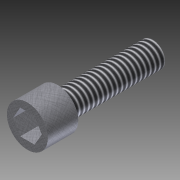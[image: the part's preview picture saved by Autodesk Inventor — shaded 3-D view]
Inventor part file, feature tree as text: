
AUTODESK INVENTOR PART (.ipt)
format: ipt  version: 2012 (Build 160160000, 160)  size: 100,864 bytes
history: native  units: in
note: dims shown in document units (in); Inventor stores cm internally (conversion verified against a paired STEP export)
features: extrude x2, sketch x1, thread x1
ambient origin geometry x8: Origin, YZ Plane, XZ Plane, XY Plane, X Axis, Y Axis, Z Axis, Center Point
bodies: Solid1 (feature_tree)
feature tree (4):
  sketch  "Sketch1"  dims[d0=0.164in d1=0.27in d2=0.625in d3=0.0in d4=0.2in d5=0.0in d6=1.0in d7=0.0in]
  extrude  "Extrusion1"  Depth=0.27in
  extrude  "Extrusion2"  Depth=0.625in TaperAngle=0.0deg
  thread  "Thread1"  [1 undecoded]
note: 1 required parameter value undecoded (feature->parameter linkage not recoverable at this tier; creation-order binding heuristic only, values carry confidence <= 0.55)
